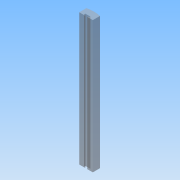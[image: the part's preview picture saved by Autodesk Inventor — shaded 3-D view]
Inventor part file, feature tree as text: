
AUTODESK INVENTOR PART (.ipt)
format: ipt  version: 2016 (Build 200138000, 138)  size: 84,480 bytes
history: native  units: mm
features: extrude x1, sketch x1
ambient origin geometry x8: Origin, YZ Plane, XZ Plane, XY Plane, X Axis, Y Axis, Z Axis, Center Point
bodies: Volumenkörper1 (feature_tree)
feature tree (2):
  extrude  "Extrusion1"  Depth=34.0mm
  sketch  "Skizze1"  dims[d2=18.0mm d3=20.0mm d4=34.0mm d5=6.2mm d6=4.6mm d7=3.0mm d8=13.0mm d9=20.0mm d10=330.0mm d11=0.0mm]
